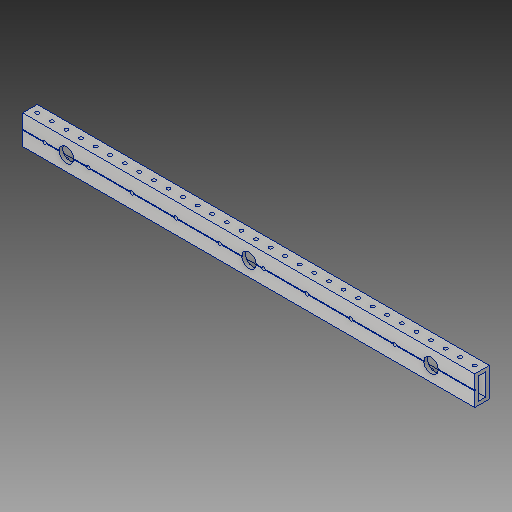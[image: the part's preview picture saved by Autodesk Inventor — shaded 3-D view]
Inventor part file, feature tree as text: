
AUTODESK INVENTOR PART (.ipt)
format: ipt  version: 2017 (Build 210142000, 142)  size: 276,992 bytes
history: native  units: in
note: dims shown in document units (in); Inventor stores cm internally (conversion verified against a paired STEP export)
features: extrude x4, sketch x4
ambient origin geometry x8: Origin, YZ Plane, XZ Plane, XY Plane, X Axis, Y Axis, Z Axis, Center Point
bodies: Solid1 (feature_tree)
feature tree (8):
  extrude  "Extrusion1"  Depth=2.0in
  extrude  "Extrusion2"  Depth=31.0in TaperAngle=0.0deg
  extrude  "Extrusion3"  Depth=1.0in
  extrude  "Extrusion4"  Depth=1.0in
  sketch  "Sketch1"  dims[d0=1.0in d1=2.0in]
  sketch  "Sketch2"  dims[d2=0.25in d3=31.0in d4=0.0in]
  sketch  "Sketch3"  dims[d5=1.0in d6=1.0in]
  sketch  "Sketch4"  dims[d7=3.0in d8=1.0in d9=3.0in d10=0.25in d11=1.5in d12=3.5433in d14=3.0in d15=0.3937in d17=1.0in d19=0.0in d20=0.0in d21=0.025in d22=0.025in d23=0.05in d24=0.0in d25=0.25in d26=0.5in d27=12.2047in d29=1.0in d30=0.3937in d32=1.0in d34=1.0in d35=0.0in]
